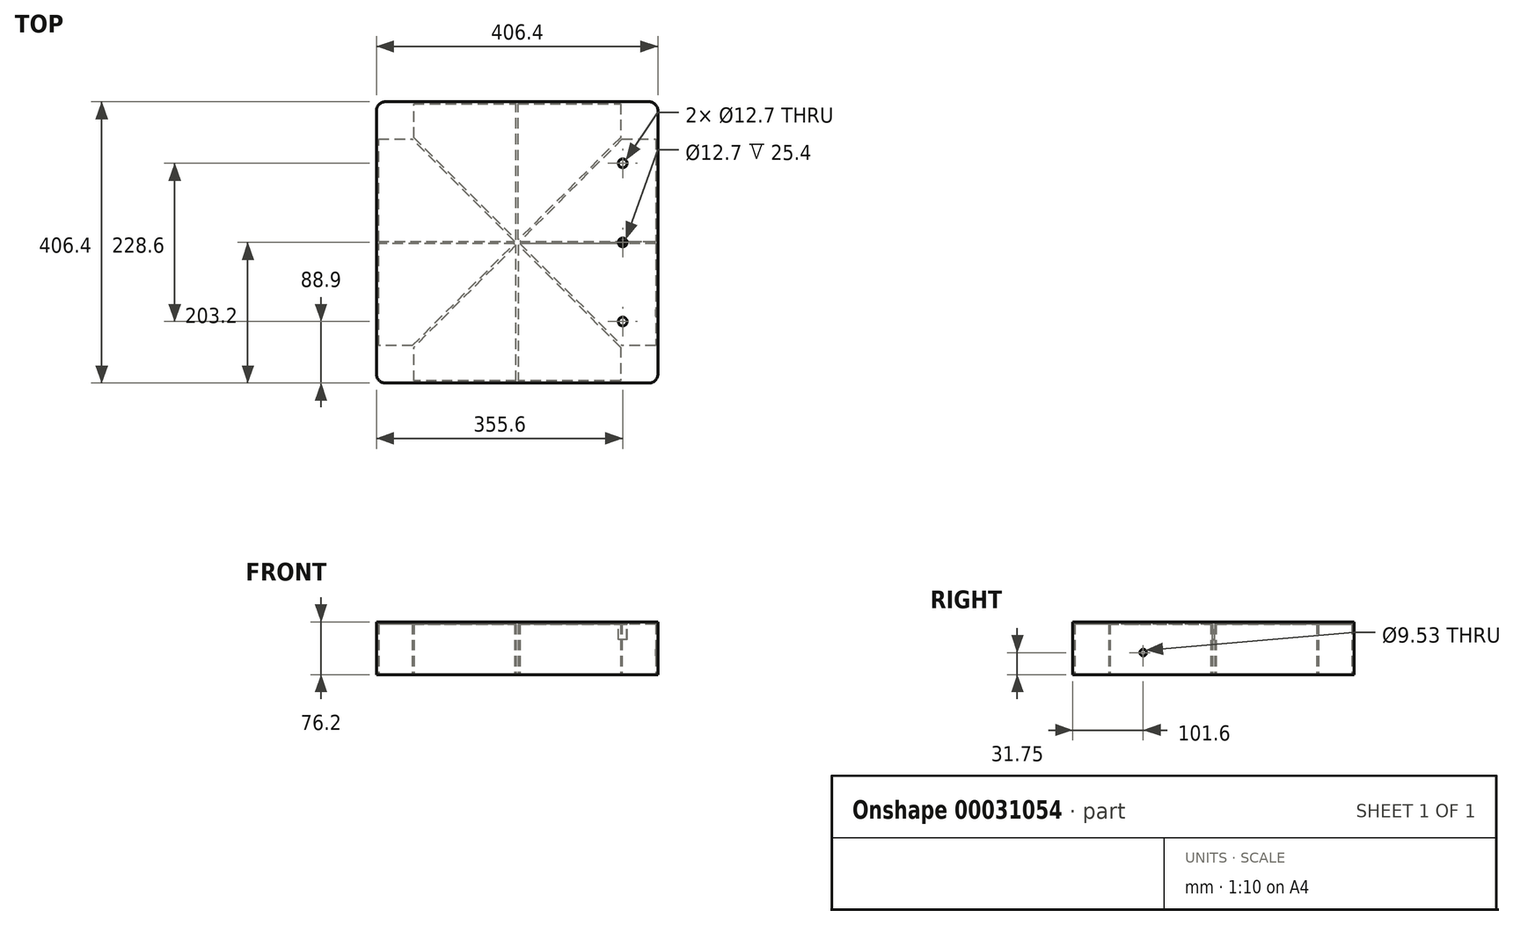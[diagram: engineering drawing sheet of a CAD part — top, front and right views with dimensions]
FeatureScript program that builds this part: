
annotation { "Feature Type Name" : "Feature", "Feature Type Description" : "" }
export const myFeature = defineFeature(function(context is Context, id is Id, definition is map)
    precondition{}
    {
        {
            var Q0;
            Q0=qCreatedBy(makeId("Top.planeOp"),FACE);
            var sketch = newSketch(context, id + "F0", { "sketchPlane" : qUnion([Q0])});
            skLineSegment(sketch, "E0.bottom", {"start": v(-203.2, 203.2) * mm, "end": v(203.2, 203.2) * mm});
            skLineSegment(sketch, "E0.top", {"start": v(-203.2, -203.2) * mm, "end": v(203.2, -203.2) * mm});
            skLineSegment(sketch, "E0.left", {"start": v(-203.2, 203.2) * mm, "end": v(-203.2, -203.2) * mm});
            skLineSegment(sketch, "E0.right", {"start": v(203.2, 203.2) * mm, "end": v(203.2, -203.2) * mm});
            skSolve(sketch);
        }
        {
            var Q0;
            Q0 = qSketchRegion(id + "F0", true);
            extrude(context, id + "F1", {"entities" : qUnion([Q0]), "depth" : 76.2 * mm});
        }
        {
            var Q0;
            Q0=makeQuery(id+"F1.opExtrude","SWEPT_EDGE",EDGE,{"disambiguationData":[OSD([sQuery(id+"F0.wireOp",EDGE,"E0.top"),sQuery(id+"F0.wireOp",EDGE,"E0.right")])]});
            var Q1;
            Q1=makeQuery(id+"F1.opExtrude","SWEPT_EDGE",EDGE,{"disambiguationData":[OSD([sQuery(id+"F0.wireOp",EDGE,"E0.top"),sQuery(id+"F0.wireOp",EDGE,"E0.left")])]});
            var Q2;
            Q2=makeQuery(id+"F1.opExtrude","SWEPT_EDGE",EDGE,{"disambiguationData":[OSD([sQuery(id+"F0.wireOp",EDGE,"E0.bottom"),sQuery(id+"F0.wireOp",EDGE,"E0.right")])]});
            var Q3;
            Q3=makeQuery(id+"F1.opExtrude","SWEPT_EDGE",EDGE,{"disambiguationData":[OSD([sQuery(id+"F0.wireOp",EDGE,"E0.bottom"),sQuery(id+"F0.wireOp",EDGE,"E0.left")])]});
            fillet(context, id + "F2", {"entities" : qUnion([Q0, Q1, Q2, Q3]), "radius" : 12.7 * mm, "tangentPropagation" : true, "allowEdgeOverflow" : false});
        }
        {
            var Q0;
            Q0=makeQuery(id+"F1.opExtrude","SWEPT_FACE",FACE,{"disambiguationData":[OSD([sQuery(id+"F0.wireOp",EDGE,"E0.right")])]});
            var sketch = newSketch(context, id + "F3", { "sketchPlane" : qUnion([Q0])});
            skCircle(sketch, "E1", {"center": v(-101.6, 31.75) * mm, "radius": 4.76 * mm});
            skSolve(sketch);
        }
        {
            var Q0;
            Q0=makeQuery(id+"F3.imprint","IMPRINT",FACE,{"disambiguationData":[TD([[makeQuery(id+"F3.imprint","IMPRINT",EDGE,{"derivedFrom":sQuery(id+"F3.wireOp",EDGE,"E1")}),1.0]])]});
            var Q1;
            Q1 = qConstructionFilter(qBodyType(qCreatedBy(id + "F3" ,EDGE), BodyType.WIRE), ConstructionObject.NO);
            extrude(context, id + "F4", {"entities" : qUnion([Q0]), "operationType" : NewBodyOperationType.REMOVE, "surfaceEntities" : qUnion([Q1]), "oppositeDirection" : true, "depth" : 25.4 * mm});
        }
        {
            var Q0;
            Q0=makeQuery(id+"F1.opExtrude","CAP_FACE",FACE,{"disambiguationData":[OSD([sQuery(id+"F0.wireOp",EDGE,"E0.bottom"),sQuery(id+"F0.wireOp",EDGE,"E0.top"),sQuery(id+"F0.wireOp",EDGE,"E0.left"),sQuery(id+"F0.wireOp",EDGE,"E0.right")])],"isStart":false});
            var sketch = newSketch(context, id + "F5", { "sketchPlane" : qUnion([Q0])});
            skCircle(sketch, "E2", {"center": v(152.4, -114.3) * mm, "radius": 6.35 * mm});
            skCircle(sketch, "E3", {"center": v(152.4, 0) * mm, "radius": 6.35 * mm});
            skCircle(sketch, "E4", {"center": v(152.4, 114.3) * mm, "radius": 6.35 * mm});
            skSolve(sketch);
        }
        {
            var Q0;
            Q0 = qSketchRegion(id + "F5", true);
            extrude(context, id + "F6", {"entities" : qUnion([Q0]), "operationType" : NewBodyOperationType.REMOVE, "oppositeDirection" : true, "depth" : 25.4 * mm});
        }
        {
            var Q0;
            Q0=makeQuery(id+"F1.opExtrude","CAP_FACE",FACE,{"disambiguationData":[OSD([sQuery(id+"F0.wireOp",EDGE,"E0.bottom"),sQuery(id+"F0.wireOp",EDGE,"E0.top"),sQuery(id+"F0.wireOp",EDGE,"E0.left"),sQuery(id+"F0.wireOp",EDGE,"E0.right")])],"isStart":true});
            var sketch = newSketch(context, id + "F7", { "sketchPlane" : qUnion([Q0])});
            skLineSegment(sketch, "E5", {"start": v(200.02, 149.22) * mm, "end": v(151.47, 149.22) * mm});
            skLineSegment(sketch, "E6", {"start": v(149.22, 151.47) * mm, "end": v(149.22, 200.02) * mm});
            skLineSegment(sketch, "E7", {"start": v(149.22, 200.02) * mm, "end": v(1.59, 200.02) * mm});
            skLineSegment(sketch, "E8", {"start": v(-149.22, 200.02) * mm, "end": v(-149.22, 151.47) * mm});
            skLineSegment(sketch, "E9", {"start": v(-151.47, 149.22) * mm, "end": v(-200.03, 149.22) * mm});
            skLineSegment(sketch, "E10", {"start": v(-200.03, 149.22) * mm, "end": v(-200.03, 1.59) * mm});
            skLineSegment(sketch, "E11", {"start": v(-200.02, -149.22) * mm, "end": v(-151.47, -149.22) * mm});
            skLineSegment(sketch, "E12", {"start": v(-149.22, -151.47) * mm, "end": v(-149.22, -200.02) * mm});
            skLineSegment(sketch, "E13", {"start": v(-149.22, -200.03) * mm, "end": v(-1.59, -200.03) * mm});
            skLineSegment(sketch, "E14", {"start": v(149.22, -200.03) * mm, "end": v(149.22, -151.47) * mm});
            skLineSegment(sketch, "E15", {"start": v(151.47, -149.23) * mm, "end": v(200.02, -149.23) * mm});
            skLineSegment(sketch, "E16", {"start": v(200.02, -149.23) * mm, "end": v(200.02, -1.59) * mm});
            skLineSegment(sketch, "E17", {"start": v(149.23, -149.23) * mm, "end": v(-149.22, 149.22) * mm, "construction": true});
            skLineSegment(sketch, "E18", {"start": v(-149.22, -149.22) * mm, "end": v(149.22, 149.22) * mm, "construction": true});
            skLineSegment(sketch, "E19", {"start": v(149.22, -151.47) * mm, "end": v(1.59, -3.83) * mm});
            skLineSegment(sketch, "E20", {"start": v(151.47, -149.23) * mm, "end": v(3.83, -1.59) * mm});
            skLineSegment(sketch, "E21", {"start": v(-149.22, -151.47) * mm, "end": v(-1.59, -3.83) * mm});
            skLineSegment(sketch, "E22", {"start": v(-1.59, -3.83) * mm, "end": v(-1.59, -200.03) * mm});
            skLineSegment(sketch, "E23", {"start": v(1.59, -3.83) * mm, "end": v(1.59, -200.03) * mm});
            skLineSegment(sketch, "E24.trimOffspring", {"start": v(1.59, -200.03) * mm, "end": v(149.22, -200.03) * mm});
            skLineSegment(sketch, "E25", {"start": v(0, 0) * mm, "end": v(0, -203.2) * mm, "construction": true});
            skLineSegment(sketch, "E26", {"start": v(0, 0) * mm, "end": v(0, 203.2) * mm, "construction": true});
            skLineSegment(sketch, "E27", {"start": v(0, 0) * mm, "end": v(-203.2, 0) * mm, "construction": true});
            skLineSegment(sketch, "E28", {"start": v(0, 0) * mm, "end": v(203.2, 0) * mm, "construction": true});
            skLineSegment(sketch, "E29", {"start": v(3.83, -1.59) * mm, "end": v(200.02, -1.59) * mm});
            skLineSegment(sketch, "E30", {"start": v(200.02, 1.59) * mm, "end": v(3.83, 1.59) * mm});
            skLineSegment(sketch, "E31", {"start": v(3.83, 1.59) * mm, "end": v(151.47, 149.22) * mm});
            skLineSegment(sketch, "E32.trimOffspring", {"start": v(200.02, 1.59) * mm, "end": v(200.02, 149.22) * mm});
            skLineSegment(sketch, "E33", {"start": v(149.22, 151.47) * mm, "end": v(1.59, 3.83) * mm});
            skLineSegment(sketch, "E34", {"start": v(1.59, 3.83) * mm, "end": v(1.59, 200.02) * mm});
            skLineSegment(sketch, "E35", {"start": v(-1.59, 200.02) * mm, "end": v(-1.59, 3.83) * mm});
            skLineSegment(sketch, "E36", {"start": v(-1.59, 3.83) * mm, "end": v(-149.22, 151.47) * mm});
            skLineSegment(sketch, "E37.trimOffspring", {"start": v(-1.59, 200.02) * mm, "end": v(-149.22, 200.02) * mm});
            skLineSegment(sketch, "E38", {"start": v(-151.47, 149.22) * mm, "end": v(-3.83, 1.59) * mm});
            skLineSegment(sketch, "E39", {"start": v(-3.83, 1.59) * mm, "end": v(-200.03, 1.59) * mm});
            skLineSegment(sketch, "E40", {"start": v(-200.03, -1.59) * mm, "end": v(-3.83, -1.59) * mm});
            skLineSegment(sketch, "E41", {"start": v(-3.83, -1.59) * mm, "end": v(-151.47, -149.22) * mm});
            skLineSegment(sketch, "E42.trimOffspring", {"start": v(-200.03, -1.59) * mm, "end": v(-200.03, -149.22) * mm});
            skSolve(sketch);
        }
        {
            var Q0;
            Q0 = qSketchRegion(id + "F7", true);
            extrude(context, id + "F8", {"entities" : qUnion([Q0]), "operationType" : NewBodyOperationType.REMOVE, "oppositeDirection" : true, "depth" : 73.02 * mm});
        }
    });
